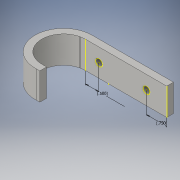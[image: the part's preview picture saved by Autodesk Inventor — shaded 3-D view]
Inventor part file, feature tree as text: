
AUTODESK INVENTOR PART (.ipt)
format: ipt  version: 2016 (Build 200138000, 138)  size: 126,976 bytes
history: native  units: in
note: dims shown in document units (in); Inventor stores cm internally (conversion verified against a paired STEP export)
features: sketch x3, extrude x2
ambient origin geometry x8: Origin, YZ Plane, XZ Plane, XY Plane, X Axis, Y Axis, Z Axis, Center Point
bodies: Solid1 (feature_tree)
feature tree (5):
  extrude  "Extrusion1"  Depth=0.25in
  extrude  "Extrusion2"  Depth=1.9994in
  sketch  "Sketch3"  dims[d11=0.7421in d12=0.25in d13=0.125in d15=1.0in d16=0.0in d17=0.25in d18=0.25in d19=0.75in d20=2.5in d21=0.25in d22=0.0in d23=0.5in d24=0.75in]
  sketch  "Sketch1"  dims[d5=0.25in d6=3.0in]
  sketch  "Sketch2"  dims[d7=3.0in d10=1.9994in]
